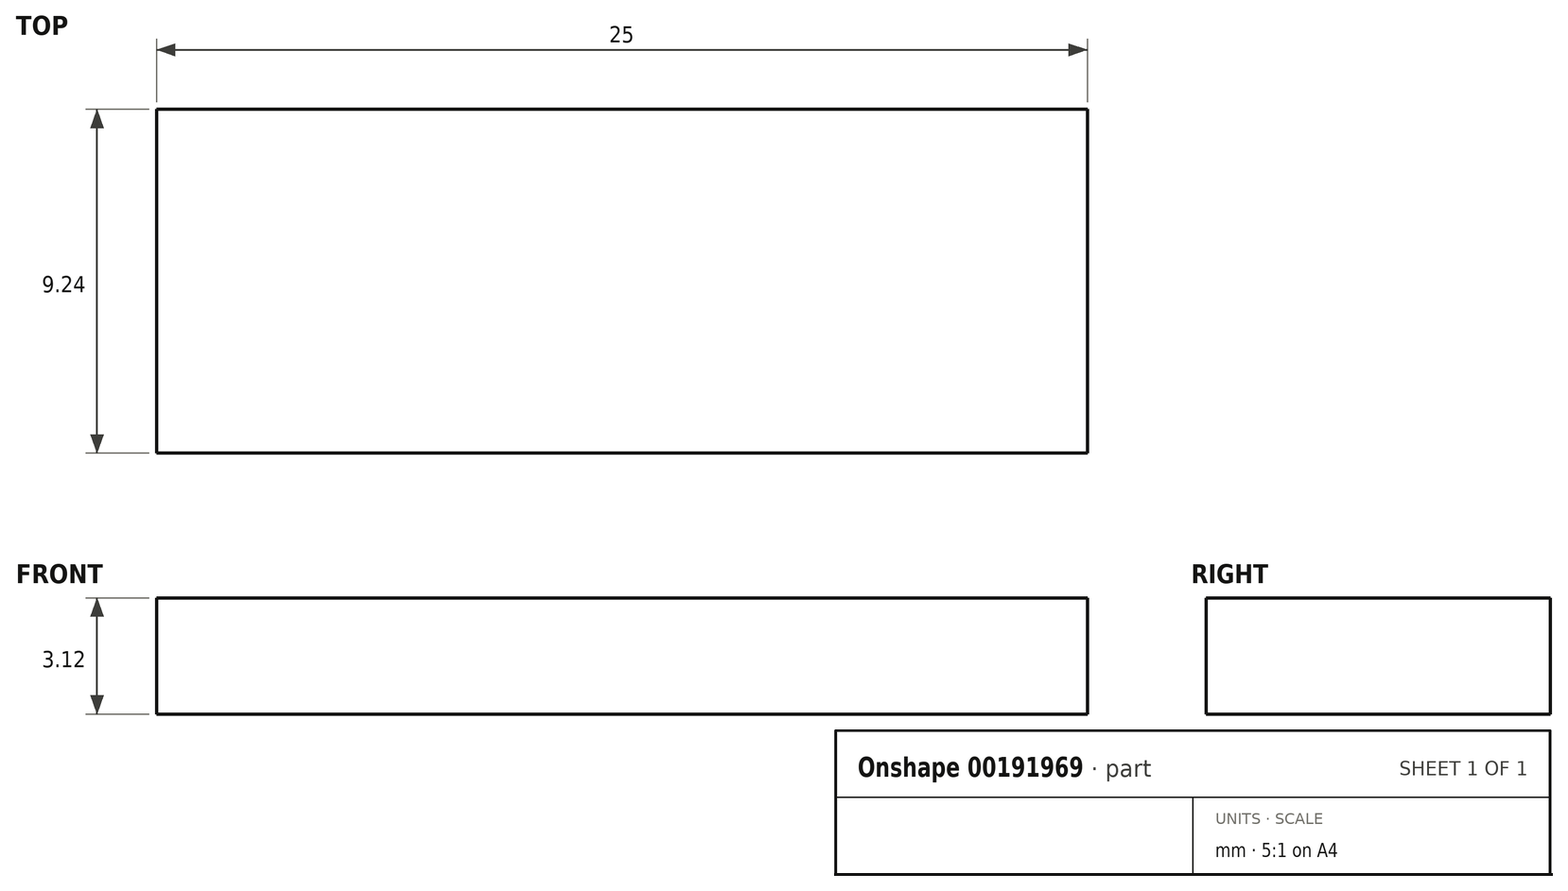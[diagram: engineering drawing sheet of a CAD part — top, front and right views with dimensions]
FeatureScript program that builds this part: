
annotation { "Feature Type Name" : "Feature", "Feature Type Description" : "" }
export const myFeature = defineFeature(function(context is Context, id is Id, definition is map)
    precondition{}
    {
        {
            var Q0;
            Q0=qCreatedBy(makeId("Top.planeOp"),FACE);
            var sketch = newSketch(context, id + "F0", { "sketchPlane" : qUnion([Q0])});
            skLineSegment(sketch, "E0.bottom", {"start": v(61.25, -28.5) * mm, "end": v(-61.25, -28.5) * mm});
            skLineSegment(sketch, "E0.top", {"start": v(61.25, 28.5) * mm, "end": v(-61.25, 28.5) * mm});
            skLineSegment(sketch, "E0.left", {"start": v(61.25, -28.5) * mm, "end": v(61.25, 28.5) * mm});
            skLineSegment(sketch, "E0.right", {"start": v(-61.25, -28.5) * mm, "end": v(-61.25, 28.5) * mm});
            skPoint(sketch, "E0.middle", {"position": v(0, 0) * mm});
            skSolve(sketch);
        }
        {
            var Q0;
            Q0 = qSketchRegion(id + "F0", true);
            extrude(context, id + "F1", {"entities" : qUnion([Q0]), "depth" : 7 * mm});
        }
        {
            var Q0;
            Q0=makeQuery(id+"F1.opExtrude","SWEPT_EDGE",EDGE,{"disambiguationData":[OSD([sQuery(id+"F0.wireOp",EDGE,"E0.bottom"),sQuery(id+"F0.wireOp",EDGE,"E0.left")])]});
            var Q1;
            Q1=makeQuery(id+"F1.opExtrude","SWEPT_EDGE",EDGE,{"disambiguationData":[OSD([sQuery(id+"F0.wireOp",EDGE,"E0.top"),sQuery(id+"F0.wireOp",EDGE,"E0.left")])]});
            var Q2;
            Q2=makeQuery(id+"F1.opExtrude","SWEPT_EDGE",EDGE,{"disambiguationData":[OSD([sQuery(id+"F0.wireOp",EDGE,"E0.bottom"),sQuery(id+"F0.wireOp",EDGE,"E0.right")])]});
            var Q3;
            Q3=makeQuery(id+"F1.opExtrude","SWEPT_EDGE",EDGE,{"disambiguationData":[OSD([sQuery(id+"F0.wireOp",EDGE,"E0.top"),sQuery(id+"F0.wireOp",EDGE,"E0.right")])]});
            fillet(context, id + "F2", {"entities" : qUnion([Q0, Q1, Q2, Q3]), "radius" : 5 * mm, "tangentPropagation" : true, "allowEdgeOverflow" : false});
        }
        {
            var Q0;
            Q0=makeQuery(id+"F1.opExtrude","SWEPT_FACE",FACE,{"disambiguationData":[OSD([sQuery(id+"F0.wireOp",EDGE,"E0.bottom")])]});
            var sketch = newSketch(context, id + "F3", { "sketchPlane" : qUnion([Q0])});
            skCircle(sketch, "E1", {"center": v(-42.91, 3.24) * mm, "radius": 2.87 * mm});
            skCircle(sketch, "E2", {"center": v(-34.87, 3.24) * mm, "radius": 3.02 * mm});
            skLineSegment(sketch, "E3.bottom", {"start": v(-47.78, 4.75) * mm, "end": v(-54.48, 4.75) * mm});
            skLineSegment(sketch, "E3.top", {"start": v(-47.78, 1.73) * mm, "end": v(-54.48, 1.73) * mm});
            skLineSegment(sketch, "E3.left", {"start": v(-47.78, 4.75) * mm, "end": v(-47.78, 1.73) * mm});
            skLineSegment(sketch, "E3.right", {"start": v(-54.48, 4.75) * mm, "end": v(-54.48, 1.73) * mm});
            skPoint(sketch, "E3.middle", {"position": v(-51.13, 3.24) * mm});
            skSolve(sketch);
        }
        {
            var Q0;
            Q0=makeQuery(id+"F1.opExtrude","SWEPT_FACE",FACE,{"disambiguationData":[OSD([sQuery(id+"F0.wireOp",EDGE,"E0.right")])]});
            var sketch = newSketch(context, id + "F4", { "sketchPlane" : qUnion([Q0])});
            skLineSegment(sketch, "E4.bottom", {"start": v(-13.34, 1.7) * mm, "end": v(-21.33, 1.7) * mm});
            skLineSegment(sketch, "E4.top", {"start": v(-13.34, 5.2) * mm, "end": v(-21.33, 5.2) * mm});
            skLineSegment(sketch, "E4.left", {"start": v(-13.34, 1.7) * mm, "end": v(-13.34, 5.2) * mm});
            skLineSegment(sketch, "E4.right", {"start": v(-21.33, 1.7) * mm, "end": v(-21.33, 5.2) * mm});
            skPoint(sketch, "E4.middle", {"position": v(-17.34, 3.45) * mm});
            skSolve(sketch);
        }
        {
            var Q0;
            Q0=makeQuery(id+"F1.opExtrude","CAP_FACE",FACE,{"disambiguationData":[OSD([sQuery(id+"F0.wireOp",EDGE,"E0.bottom"),sQuery(id+"F0.wireOp",EDGE,"E0.top"),sQuery(id+"F0.wireOp",EDGE,"E0.left"),sQuery(id+"F0.wireOp",EDGE,"E0.right")])],"isStart":false});
            var sketch = newSketch(context, id + "F5", { "sketchPlane" : qUnion([Q0])});
            skLineSegment(sketch, "E5.bottom", {"start": v(48.1, 20.68) * mm, "end": v(-49.57, 20.68) * mm});
            skLineSegment(sketch, "E5.top", {"start": v(48.1, -21.26) * mm, "end": v(-49.57, -21.26) * mm});
            skLineSegment(sketch, "E5.left", {"start": v(48.1, 20.68) * mm, "end": v(48.1, -21.26) * mm});
            skLineSegment(sketch, "E5.right", {"start": v(-49.57, 20.68) * mm, "end": v(-49.57, -21.26) * mm});
            skCircle(sketch, "E6", {"center": v(54.26, -0.3) * mm, "radius": 4.41 * mm});
            skPoint(sketch, "E6.centerSnap0", {"position": v(48.1, -0.3) * mm});
            skSolve(sketch);
        }
        {
            var Q0;
            Q0 = qSketchRegion(id + "F4", true);
            extrude(context, id + "F6", {"entities" : qUnion([Q0]), "operationType" : NewBodyOperationType.ADD, "depth" : 0.75 * mm});
        }
        {
            var Q0;
            Q0 = qSketchRegion(id + "F3", true);
            extrude(context, id + "F7", {"entities" : qUnion([Q0]), "operationType" : NewBodyOperationType.ADD, "depth" : 0.75 * mm});
        }
        {
            var Q0;
            Q0=makeQuery(id+"F5.imprint","IMPRINT",FACE,{"disambiguationData":[TD([[makeQuery(id+"F5.imprint","IMPRINT",EDGE,{"derivedFrom":sQuery(id+"F5.wireOp",EDGE,"E6")}),1.0]])]});
            var Q1;
            Q1=sQuery(id+"F5.wireOp",EDGE,"E6");
            extrude(context, id + "F8", {"entities" : qUnion([Q0]), "operationType" : NewBodyOperationType.REMOVE, "surfaceEntities" : qUnion([Q1]), "oppositeDirection" : true, "depth" : 0.5 * mm});
        }
        {
            var Q0;
            Q0=makeQuery(id+"F8.boolean.opBoolean","COPY",FACE,{"derivedFrom":makeQuery(id+"F8.opExtrude","CAP_FACE",FACE,{"disambiguationData":[OSD([sQuery(id+"F5.wireOp",EDGE,"E6")])],"isStart":false})});
            fillet(context, id + "F9", {"entities" : qUnion([Q0]), "radius" : 1 * mm, "tangentPropagation" : true, "allowEdgeOverflow" : false});
        }
        {
            var Q0;
            Q0=makeQuery(id+"F1.opExtrude","SWEPT_FACE",FACE,{"disambiguationData":[OSD([sQuery(id+"F0.wireOp",EDGE,"E0.left")])]});
            var sketch = newSketch(context, id + "F10", { "sketchPlane" : qUnion([Q0])});
            skLineSegment(sketch, "E7.bottom", {"start": v(-5.82, 4.75) * mm, "end": v(5.11, 4.75) * mm});
            skLineSegment(sketch, "E7.top", {"start": v(-5.82, 2.2) * mm, "end": v(5.11, 2.2) * mm});
            skLineSegment(sketch, "E7.left", {"start": v(-5.82, 4.75) * mm, "end": v(-5.82, 2.2) * mm});
            skLineSegment(sketch, "E7.right", {"start": v(5.11, 4.75) * mm, "end": v(5.11, 2.2) * mm});
            skSolve(sketch);
        }
        {
            var Q0;
            Q0 = qSketchRegion(id + "F10", true);
            extrude(context, id + "F11", {"entities" : qUnion([Q0]), "operationType" : NewBodyOperationType.ADD, "oppositeDirection" : true, "depth" : 1 * mm});
        }
        {
            var Q0;
            Q0=makeQuery(id+"F1.opExtrude","SWEPT_FACE",FACE,{"disambiguationData":[OSD([sQuery(id+"F0.wireOp",EDGE,"E0.left")])]});
            var sketch = newSketch(context, id + "F12", { "sketchPlane" : qUnion([Q0])});
            skCircle(sketch, "E8", {"center": v(16.86, 3.7) * mm, "radius": 2.47 * mm});
            skSolve(sketch);
        }
        {
            var Q0;
            Q0=makeQuery(id+"F12.imprint","IMPRINT",FACE,{"disambiguationData":[TD([[makeQuery(id+"F12.imprint","IMPRINT",EDGE,{"derivedFrom":sQuery(id+"F12.wireOp",EDGE,"E8")}),1.0]])]});
            extrude(context, id + "F13", {"entities" : qUnion([Q0]), "operationType" : NewBodyOperationType.REMOVE, "oppositeDirection" : true, "depth" : 7 * mm});
        }
        {
            var Q0;
            Q0=makeQuery(id+"F1.opExtrude","SWEPT_FACE",FACE,{"disambiguationData":[OSD([sQuery(id+"F0.wireOp",EDGE,"E0.left")])]});
            var sketch = newSketch(context, id + "F14", { "sketchPlane" : qUnion([Q0])});
            skLineSegment(sketch, "E9.bottom", {"start": v(4.62, 2.04) * mm, "end": v(-4.62, 2.04) * mm});
            skLineSegment(sketch, "E9.top", {"start": v(4.62, 5.16) * mm, "end": v(-4.62, 5.16) * mm});
            skLineSegment(sketch, "E9.left", {"start": v(4.62, 2.04) * mm, "end": v(4.62, 5.16) * mm});
            skLineSegment(sketch, "E9.right", {"start": v(-4.62, 2.04) * mm, "end": v(-4.62, 5.16) * mm});
            skPoint(sketch, "E9.middle", {"position": v(0, 3.6) * mm});
            skCircle(sketch, "E10", {"center": v(-8.46, 3.6) * mm, "radius": 1.37 * mm});
            skCircle(sketch, "E11", {"center": v(7.75, 3.6) * mm, "radius": 1.37 * mm});
            skPoint(sketch, "E11.centerSnap0", {"position": v(4.62, 3.6) * mm});
            skSolve(sketch);
        }
        {
            var Q0;
            Q0=makeQuery(id+"F14.imprint","IMPRINT",FACE,{"disambiguationData":[TD([[makeQuery(id+"F14.imprint","IMPRINT",EDGE,{"derivedFrom":sQuery(id+"F14.wireOp",EDGE,"E9.bottom")}),-1.0]])]});
            extrude(context, id + "F15", {"entities" : qUnion([Q0]), "operationType" : NewBodyOperationType.INTERSECT, "oppositeDirection" : true, "depth" : 25 * mm});
        }
    });
